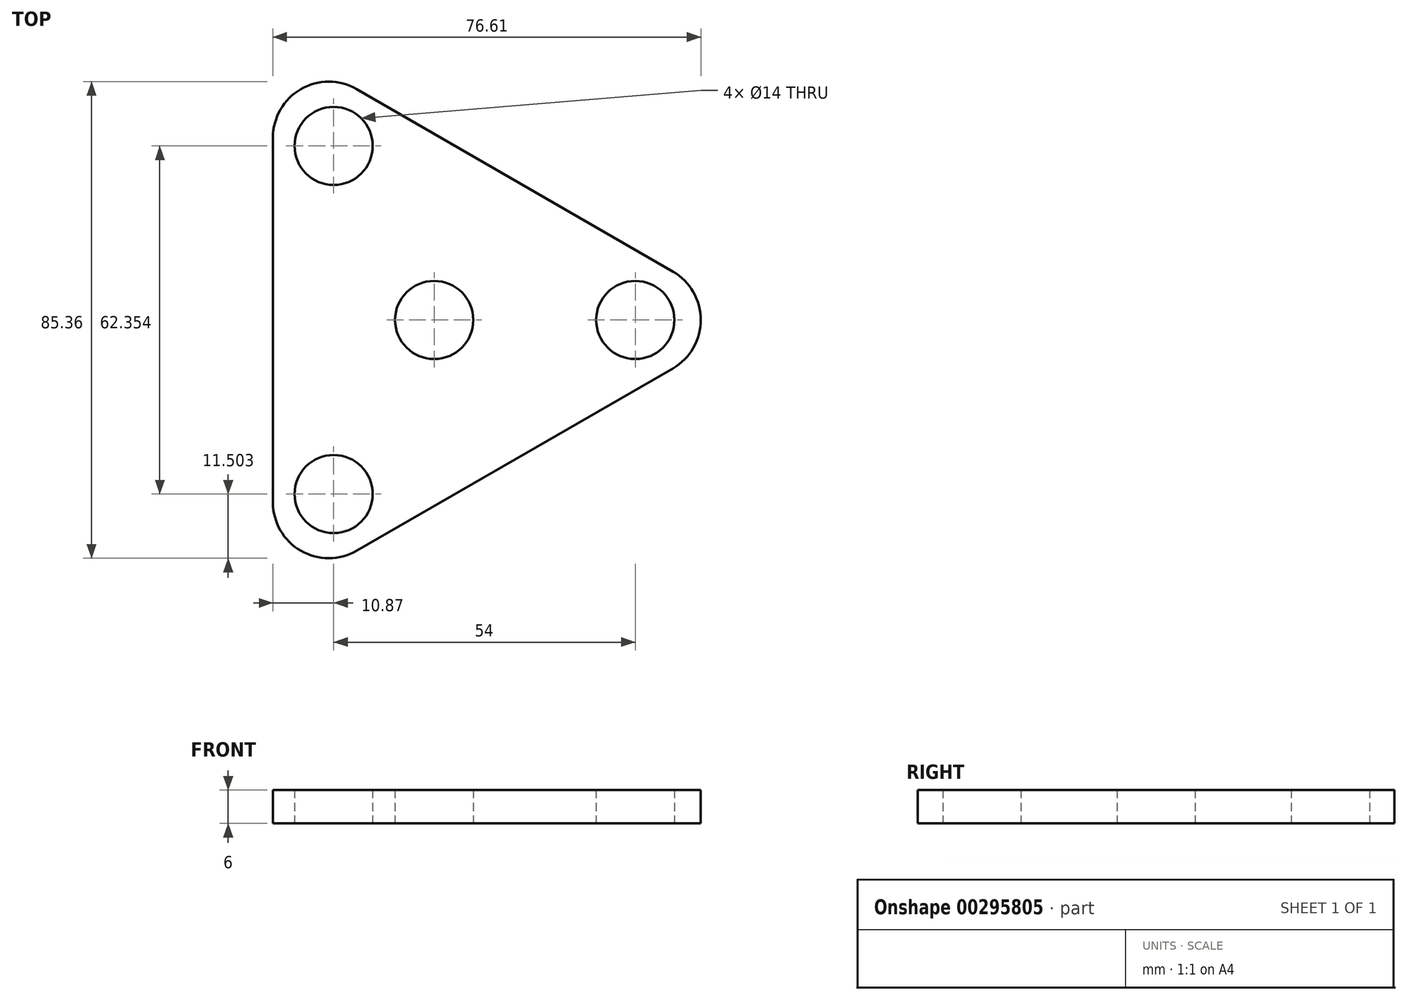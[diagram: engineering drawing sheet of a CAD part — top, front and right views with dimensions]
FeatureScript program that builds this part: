
annotation { "Feature Type Name" : "Feature", "Feature Type Description" : "" }
export const myFeature = defineFeature(function(context is Context, id is Id, definition is map)
    precondition{}
    {
        {
            var Q0;
            Q0=qCreatedBy(makeId("Top.planeOp"),FACE);
            var sketch = newSketch(context, id + "F0", { "sketchPlane" : qUnion([Q0])});
            skCircle(sketch, "E0.cCircle", {"center": v(0, 0) * mm, "radius": 28.87 * mm, "construction": true});
            skLineSegment(sketch, "E0.0", {"start": v(-28.87, -50) * mm, "end": v(-28.87, 50) * mm});
            skLineSegment(sketch, "E0.1", {"start": v(-28.87, 50) * mm, "end": v(57.74, 0) * mm});
            skLineSegment(sketch, "E0.2", {"start": v(57.74, 0) * mm, "end": v(-28.87, -50) * mm});
            skPoint(sketch, "E0.0.midPoint", {"position": v(-28.87, 0) * mm});
            skLineSegment(sketch, "E1", {"start": v(0, 0) * mm, "end": v(57.74, 0) * mm, "construction": true});
            skCircle(sketch, "E2", {"center": v(36, 0) * mm, "radius": 7 * mm});
            skCircle(sketch, "E3.1.0", {"center": v(-18, 31.18) * mm, "radius": 7 * mm});
            skCircle(sketch, "E3.2.0", {"center": v(-18, -31.18) * mm, "radius": 7 * mm});
            skCircle(sketch, "E4", {"center": v(0, 0) * mm, "radius": 7 * mm});
            skSolve(sketch);
        }
        {
            var Q0;
            Q0=qSketchRegion(id+"F0",true);
            extrude(context, id + "F1", {"entities" : qUnion([Q0]), "depth" : 6 * mm});
        }
        {
            var Q0;
            Q0=makeQuery(id+"F1.opExtrude","SWEPT_EDGE",EDGE,{"disambiguationData":[OSD([sQuery(id+"F0.wireOp",EDGE,"E0.0"),sQuery(id+"F0.wireOp",EDGE,"E0.2")])]});
            var Q1;
            Q1=makeQuery(id+"F1.opExtrude","SWEPT_EDGE",EDGE,{"disambiguationData":[OSD([sQuery(id+"F0.wireOp",EDGE,"E0.1"),sQuery(id+"F0.wireOp",EDGE,"E0.2")])]});
            var Q2;
            Q2=makeQuery(id+"F1.opExtrude","SWEPT_EDGE",EDGE,{"disambiguationData":[OSD([sQuery(id+"F0.wireOp",EDGE,"E0.0"),sQuery(id+"F0.wireOp",EDGE,"E0.1")])]});
            fillet(context, id + "F2", {"entities" : qUnion([Q0, Q1, Q2]), "radius" : 10 * mm, "tangentPropagation" : true, "allowEdgeOverflow" : false});
        }
    });
